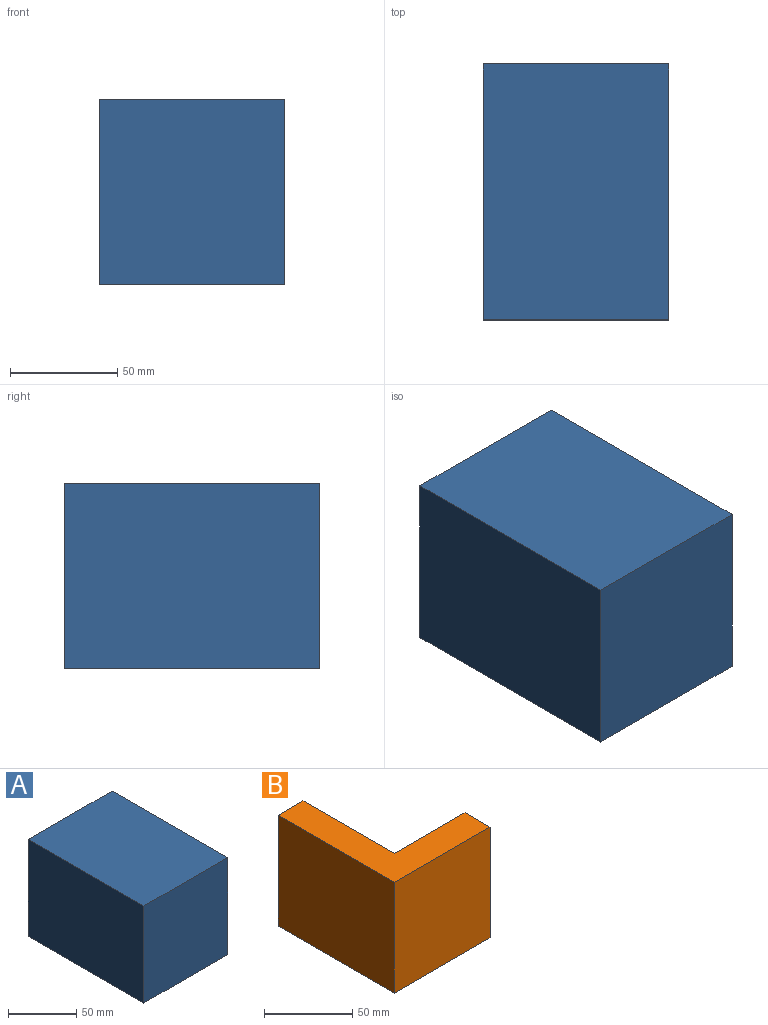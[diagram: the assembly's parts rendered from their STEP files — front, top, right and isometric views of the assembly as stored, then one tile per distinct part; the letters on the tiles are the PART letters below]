
ASSEMBLY  parts=2 mates=1
PART A: 141 faces, bbox 91x119.9x91 mm
  f0: plane 114.49x69.64mm, normal (-1,0,0), area 5760.8mm2, adj f2,f3,f4,f5,f6,f7,f8,f9
  f1: plane 114.87x69.86mm, normal (0,0,-1), area 5819.2mm2, adj f11,f12,f13,f17,f100,f101,f102,f103
  f2: plane 47.66x8.91mm, normal (0.71,0,-0.71), area 558.5mm2, adj f0,f5,f10,f55,f56,f57,f60,f66
  f3: plane 10.21x9.31mm, normal (0.67,-0.32,-0.67), area 53.6mm2, adj f0,f5,f6,f44,f68
  f4: cylinder r=2mm len=29.58mm, axis (0,0,-1), area 38.8mm2, adj f0,f7,f15,f18
  f5: cylinder r=4mm len=8.9mm, axis (0.71,0,0.71), area 15.8mm2, adj f0,f2,f3,f67
  f6: cylinder r=4mm len=1.37mm, axis (0.31,0.94,-0.13), area 0.5mm2, adj f0,f3,f7
  f7: bspline ~2.68x2.45mm, area 4mm2, adj f0,f4,f6,f18,f44
  f8: bspline ~42.11x4.6mm, area 6.8mm2, adj f0,f9,f16,f25
  f9: sphere r=3mm, area 0mm2, adj f0,f8,f10
  f10: bspline ~26.92x26.92mm, area 54.6mm2, adj f0,f2,f9,f25,f94
  f11: plane 47.66x7.72mm, normal (0.71,0,0.71), area 519.4mm2, adj f0,f1,f13,f17
  f12: plane 9.46x9.31mm, normal (0.67,-0.32,0.67), area 52.4mm2, adj f0,f1,f13,f14,f106,f110
  f13: cylinder r=4mm len=8.15mm, axis (0.71,0,-0.71), area 14.3mm2, adj f0,f1,f11,f12
  f14: cylinder r=4mm len=1.37mm, axis (0.31,0.94,0.13), area 0.5mm2, adj f0,f12,f15
  f15: bspline ~2.68x2.45mm, area 4mm2, adj f0,f4,f14,f18,f106
  f16: sphere r=3mm, area 0mm2, adj f0,f8,f17
  f17: bspline ~26.92x26.92mm, area 50.7mm2, adj f0,f1,f11,f16,f25,f126
  f18: plane 51.12x51.12mm, normal (0,-1,0), area 603.6mm2, adj f4,f7,f15,f32,f41,f42,f43,f44
  f19: torus R=0.76mm, axis (0,0,1), area 3.2mm2, adj f40,f49,f52,f57,f58,f65
  f20: plane 31.1x2.5mm, normal (0,0,-1), area 70.7mm2, adj f58,f59,f62,f66,f80
  f21: plane 34.04x9.66mm, normal (-0.71,0,-0.71), area 464.9mm2, adj f46,f51,f77,f87
  f22: plane 10.24x10.24mm, normal (-0.71,0,-0.71), area 32.9mm2, adj f63,f72,f80,f90
  f23: plane 34.04x30.69mm, normal (-1,0,0), area 1044.5mm2, adj f45,f50,f87,f119
  f24: plane 31.51x2.27mm, normal (-1,0,0), area 71.5mm2, adj f64,f73,f90,f122
  f25: cone r=74.82mm half-angle=77.1deg, axis (0,-1,0), area 1127.5mm2, adj f8,f10,f17,f31,f95,f97,f99,f127
  f26: plane 31.52x5.53mm, normal (-1,0,0), area 163.3mm2, adj f71,f84,f99,f116
  f27: torus R=3.33mm, axis (0,-1,0), area 98.8mm2, adj f28,f34
  f28: plane 6.67x6.67mm, normal (0,-1,0), area 34.9mm2, adj f27
  f29: plane 37x37mm, normal (0,1,0), area 1075.2mm2, adj f30
  f30: cylinder r=18.5mm len=37mm, axis (0,-1,0), area 3372.5mm2, adj f29,f31
  f31: torus R=23.5mm, axis (0,-1,0), area 840.6mm2, adj f25,f30
  f32: cone r=10.5mm half-angle=86.5deg, axis (0,-1,0), area 1466.1mm2, adj f18,f33
  f33: torus R=10.8mm, axis (0,-1,0), area 166.6mm2, adj f32,f34
  f34: cone r=6.33mm half-angle=53.1deg, axis (0,-1,0), area 81.4mm2, adj f27,f33
  f35: plane 31.52x5.93mm, normal (0,0,-1), area 163.5mm2, adj f53,f54,f60,f74,f95
  f36: plane 10.25x10.25mm, normal (-0.71,0,-0.71), area 67.4mm2, adj f70,f74,f84,f97
  f37: plane 31.08x4.02mm, normal (0,-0.32,-0.95), area 129.2mm2, adj f43,f62,f68,f82
  f38: plane 10.77x10.77mm, normal (-0.67,-0.32,-0.67), area 58.8mm2, adj f42,f63,f82,f92
  f39: plane 31.47x4.02mm, normal (-0.95,-0.32,0), area 130.9mm2, adj f41,f64,f92,f124
  f40: plane 34.04x30.11mm, normal (0,0,-1), area 1024.6mm2, adj f19,f47,f48,f49,f52,f77
  f41: cylinder r=2mm len=30.36mm, axis (0,0,-1), area 75.8mm2, adj f18,f39,f93,f125
  f42: cylinder r=2mm len=10.77mm, axis (-0.71,0,0.71), area 33.3mm2, adj f18,f38,f83,f93
  f43: cylinder r=2mm len=29.97mm, axis (-1,0,0), area 74.9mm2, adj f18,f37,f69,f83
  f44: cylinder r=2mm len=10.21mm, axis (0.71,0,0.71), area 31.3mm2, adj f3,f7,f18,f69
  f45: cylinder r=3mm len=31.51mm, axis (0,0,-1), area 54.6mm2, adj f23,f71,f86,f118
  f46: cylinder r=3mm len=10.6mm, axis (-0.71,0,0.71), area 24.7mm2, adj f21,f70,f76,f86
  f47: cylinder r=3mm len=29.76mm, axis (-1,0,0), area 51.9mm2, adj f40,f48,f53,f76
  f48: torus R=0.76mm, axis (0,0,1), area 3.4mm2, adj f40,f47,f49,f54,f55
  f49: cylinder r=3mm len=32.51mm, axis (0,-1,0), area 28.6mm2, adj f19,f40,f48,f56
  f50: cylinder r=3mm len=31.51mm, axis (0,0,-1), area 54.6mm2, adj f23,f73,f88,f120
  f51: cylinder r=3mm len=10.6mm, axis (-0.71,0,0.71), area 24.7mm2, adj f21,f72,f78,f88
  f52: cylinder r=3mm len=29.76mm, axis (-1,0,0), area 51.9mm2, adj f19,f40,f59,f78
  f53: cylinder r=3mm len=29.76mm, axis (-1,0,0), area 52.3mm2, adj f35,f47,f54,f75
  f54: torus R=4.08mm, axis (0,0,-1), area 2.5mm2, adj f35,f48,f53,f61
  f55: bspline ~5.3x3.85mm, area 10mm2, adj f2,f48,f56,f61
  f56: cylinder r=3mm len=32.51mm, axis (0,-1,0), area 105.2mm2, adj f2,f49,f55,f57
  f57: bspline ~4.49x3.57mm, area 7.8mm2, adj f2,f19,f56,f65
  f58: torus R=4.08mm, axis (0,0,-1), area 1.9mm2, adj f19,f20,f59,f65
  f59: cylinder r=3mm len=29.76mm, axis (-1,0,0), area 52.3mm2, adj f20,f52,f58,f79
  f60: cylinder r=3mm len=4.92mm, axis (0,1,0), area 11.6mm2, adj f2,f35,f61,f94
  f61: sphere r=3mm, area 2.1mm2, adj f54,f55,f60
  f62: cylinder r=4mm len=31.1mm, axis (1,0,0), area 40mm2, adj f20,f37,f67,f81
  f63: cylinder r=4mm len=10.39mm, axis (0.71,0,-0.71), area 18.6mm2, adj f22,f38,f81,f91
  f64: cylinder r=4mm len=31.51mm, axis (0,0,-1), area 40.5mm2, adj f24,f39,f91,f123
  f65: bspline ~3.82x2.29mm, area 4.4mm2, adj f19,f57,f58,f66
  f66: cylinder r=4mm len=3.4mm, axis (0,1,0), area 9.3mm2, adj f2,f20,f65,f67
  f67: sphere r=4mm, area 5.3mm2, adj f5,f62,f66,f68
  f68: cylinder r=4mm len=4.11mm, axis (0.13,0.94,-0.31), area 12.7mm2, adj f3,f37,f67,f69
  f69: bspline ~2.68x2.45mm, area 5.8mm2, adj f18,f43,f44,f68
  f70: cylinder r=3mm len=10.6mm, axis (-0.71,0,0.71), area 25.5mm2, adj f36,f46,f75,f85
  f71: cylinder r=3mm len=31.51mm, axis (0,0,-1), area 55.4mm2, adj f26,f45,f85,f117
  f72: cylinder r=3mm len=10.6mm, axis (-0.71,0,0.71), area 25.5mm2, adj f22,f51,f79,f89
  f73: cylinder r=3mm len=31.51mm, axis (0,0,-1), area 55.4mm2, adj f24,f50,f89,f121
  f74: cylinder r=3mm len=4.52mm, axis (0,1,0), area 10.7mm2, adj f35,f36,f75,f96
  f75: sphere r=3mm, area 4.4mm2, adj f53,f70,f74,f76
  f76: bspline ~2.19x2.14mm, area 3.8mm2, adj f46,f47,f75,f77
  f77: cylinder r=3mm len=34.04mm, axis (0,-1,0), area 80.2mm2, adj f21,f40,f76,f78
  f78: bspline ~2.19x1.85mm, area 3.8mm2, adj f51,f52,f77,f79
  f79: sphere r=3mm, area 5.2mm2, adj f59,f72,f78,f80
  f80: cylinder r=3mm len=2.27mm, axis (0,1,0), area 5.3mm2, adj f20,f22,f79,f81
  f81: bspline ~2.41x2.16mm, area 3.1mm2, adj f62,f63,f80,f82
  f82: cylinder r=3mm len=4.09mm, axis (0.13,-0.94,0.31), area 9.5mm2, adj f37,f38,f81,f83
  f83: bspline ~2.18x2.01mm, area 3.9mm2, adj f18,f42,f43,f82
  f84: cylinder r=3mm len=4.52mm, axis (0,1,0), area 10.7mm2, adj f26,f36,f85,f98
  f85: sphere r=3mm, area 3.9mm2, adj f70,f71,f84,f86
  f86: bspline ~2.19x2.14mm, area 3.8mm2, adj f45,f46,f85,f87
  f87: cylinder r=3mm len=34.04mm, axis (0,-1,0), area 80.2mm2, adj f21,f23,f86,f88
  f88: bspline ~2.19x1.85mm, area 3.8mm2, adj f50,f51,f87,f89
  f89: sphere r=3mm, area 3.9mm2, adj f72,f73,f88,f90
  f90: cylinder r=3mm len=2.27mm, axis (0,1,0), area 5.3mm2, adj f22,f24,f89,f91
  f91: bspline ~2.41x2.16mm, area 3.1mm2, adj f63,f64,f90,f92
  f92: cylinder r=3mm len=4.09mm, axis (-0.31,0.94,-0.13), area 9.5mm2, adj f38,f39,f91,f93
  f93: bspline ~2.18x2.01mm, area 3.9mm2, adj f18,f41,f42,f92
  f94: sphere r=3mm, area 5.7mm2, adj f10,f60,f95
  f95: bspline ~42.55x4.6mm, area 130.4mm2, adj f25,f35,f94,f96
  f96: sphere r=3mm, area 7mm2, adj f74,f95,f97
  f97: bspline ~26.92x26.92mm, area 59.4mm2, adj f25,f36,f96,f98
  f98: sphere r=3mm, area 4.6mm2, adj f84,f97,f99
  f99: bspline ~42.11x4.6mm, area 130.4mm2, adj f25,f26,f98,f130
  f100: plane 34.04x9.47mm, normal (-0.71,0,0.71), area 455.8mm2, adj f1,f107,f108,f119
  f101: plane 9.05x9.05mm, normal (-0.71,0,0.71), area 29.1mm2, adj f1,f109,f113,f122
  f102: plane 9.06x9.06mm, normal (-0.71,0,0.71), area 59.7mm2, adj f1,f112,f116,f129
  f103: plane 10.77x9.74mm, normal (-0.67,-0.32,0.67), area 56.4mm2, adj f1,f104,f109,f114,f124
  f104: cylinder r=2mm len=10.77mm, axis (-0.71,0,-0.71), area 33.3mm2, adj f18,f103,f115,f125
  f105: cylinder r=2mm len=29.97mm, axis (-1,0,0), area 45.4mm2, adj f1,f18,f111,f115
  f106: cylinder r=2mm len=10.21mm, axis (0.71,0,-0.71), area 31.3mm2, adj f12,f15,f18,f111
  f107: cylinder r=3mm len=10.11mm, axis (-0.71,0,-0.71), area 23.5mm2, adj f1,f100,f112,f118
  f108: cylinder r=3mm len=10.11mm, axis (-0.71,0,-0.71), area 23.5mm2, adj f1,f100,f113,f120
  f109: cylinder r=4mm len=9.34mm, axis (0.71,0,0.71), area 16.6mm2, adj f1,f101,f103,f123
  f110: cylinder r=4mm len=1.85mm, axis (0.13,0.94,0.31), area 0.9mm2, adj f1,f12,f111
  f111: bspline ~2.68x2.45mm, area 4.9mm2, adj f1,f18,f105,f106,f110
  f112: cylinder r=3mm len=9.76mm, axis (-0.71,0,-0.71), area 22.9mm2, adj f1,f102,f107,f117
  f113: cylinder r=3mm len=9.76mm, axis (-0.71,0,-0.71), area 22.9mm2, adj f1,f101,f108,f121
  f114: cylinder r=3mm len=0.98mm, axis (0.13,-0.94,-0.31), area 0.2mm2, adj f1,f103,f115
  f115: bspline ~2.18x2.01mm, area 2.8mm2, adj f1,f18,f104,f105,f114
  f116: cylinder r=3mm len=4.52mm, axis (0,1,0), area 10.7mm2, adj f26,f102,f117,f130
  f117: sphere r=3mm, area 3.9mm2, adj f71,f112,f116,f118
  f118: bspline ~2.19x2.14mm, area 3.8mm2, adj f45,f107,f117,f119
  f119: cylinder r=3mm len=34.04mm, axis (0,-1,0), area 80.2mm2, adj f23,f100,f118,f120
  f120: bspline ~2.19x1.85mm, area 3.8mm2, adj f50,f108,f119,f121
  f121: sphere r=3mm, area 3.9mm2, adj f73,f113,f120,f122
  f122: cylinder r=3mm len=2.27mm, axis (0,1,0), area 5.3mm2, adj f24,f101,f121,f123
  f123: bspline ~2.41x2.16mm, area 3.1mm2, adj f64,f109,f122,f124
  f124: cylinder r=3mm len=4.09mm, axis (-0.31,0.94,0.13), area 9.5mm2, adj f39,f103,f123,f125
  f125: bspline ~2.18x2.01mm, area 3.9mm2, adj f18,f41,f104,f124
  f126: sphere r=3mm, area 0.1mm2, adj f1,f17,f127
  f127: bspline ~38.68x4.6mm, area 11.9mm2, adj f1,f25,f126,f128
  f128: sphere r=3mm, area 0.1mm2, adj f1,f127,f129
  f129: bspline ~26.92x26.92mm, area 55.4mm2, adj f1,f25,f102,f128,f130
  f130: sphere r=3mm, area 4.6mm2, adj f99,f116,f129
  f131: plane 86.76x86.6mm, normal (0,1,0), area 1660.3mm2, adj f0,f1,f132,f133,f134,f135,f136,f137
  f132: plane 119.3x86.6mm, normal (0,0,1), area 10331.7mm2, adj f131,f133,f135,f140
  f133: plane 119.3x86.76mm, normal (-1,0,0), area 10350mm2, adj f131,f132,f134,f140
  f134: plane 119.3x86.6mm, normal (0,0,-1), area 10331.7mm2, adj f131,f133,f135,f140
  f135: plane 119.3x86.76mm, normal (1,0,0), area 10350mm2, adj f131,f132,f134,f140
  f136: plane 114.3x76.6mm, normal (0,0,1), area 8755.7mm2, adj f0,f131,f137,f139
  f137: plane 114.3x76.76mm, normal (1,0,0), area 8773.2mm2, adj f1,f131,f136,f139
  f138: plane 114.3x7.31mm, normal (-0.71,0,-0.71), area 1182mm2, adj f0,f1,f131,f139
  f139: plane 76.76x76.6mm, normal (0,1,0), area 5853mm2, adj f0,f1,f136,f137,f138
  f140: plane 86.76x86.6mm, normal (0,-1,0), area 7513.3mm2, adj f132,f133,f134,f135
PART B: 9 faces, bbox 76.6x93x76.8 mm
  f0: plane 93x76.6mm, normal (0,0,1), area 2992mm2, adj f1,f3,f4,f5,f6,f8
  f1: plane 93x76.76mm, normal (-1,0,0), area 7138.3mm2, adj f0,f2,f4,f8
  f2: plane 93x76.6mm, normal (0,0,-1), area 7124mm2, adj f1,f3,f4,f8
  f3: plane 93x76.76mm, normal (1,0,0), area 2995.1mm2, adj f0,f2,f4,f5,f7,f8
  f4: plane 76.76x76.6mm, normal (0,-1,0), area 5879.7mm2, adj f0,f1,f2,f3
  f5: plane 56.76x56.6mm, normal (0,1,0), area 3212.5mm2, adj f0,f3,f6,f7
  f6: plane 73x56.76mm, normal (1,0,0), area 4143.2mm2, adj f0,f5,f7,f8
  f7: plane 73x56.6mm, normal (0,0,1), area 4132mm2, adj f3,f5,f6,f8
  f8: plane 76.76x76.6mm, normal (0,1,0), area 2667.2mm2, adj f0,f1,f2,f3,f6,f7
PLACE A t=(8,-40.28,30.32)mm
PLACE B t=(7.84,-40.28,30.16)mm
MATE planar B.f4 <-> A.f139  axis (0,-1,0) through (-3.68,-57.28,18.71)mm
